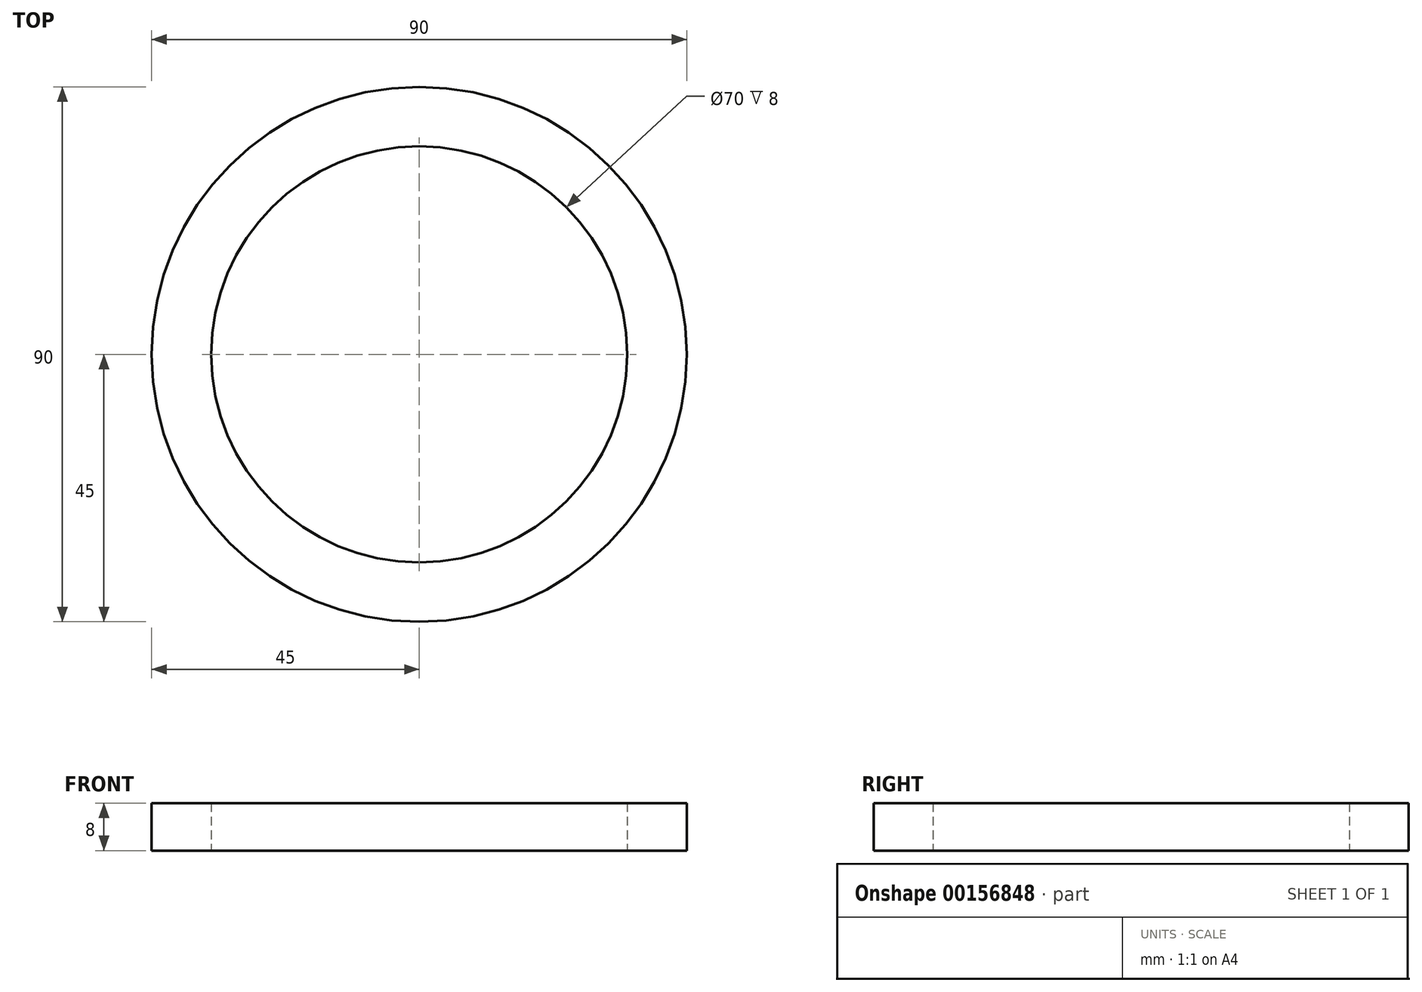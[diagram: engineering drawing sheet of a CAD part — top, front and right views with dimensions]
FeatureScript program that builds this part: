
annotation { "Feature Type Name" : "Feature", "Feature Type Description" : "" }
export const myFeature = defineFeature(function(context is Context, id is Id, definition is map)
    precondition{}
    {
        {
            var Q0;
            Q0=qCreatedBy(makeId("Top.planeOp"),FACE);
            var sketch = newSketch(context, id + "F0", { "sketchPlane" : qUnion([Q0])});
            skCircle(sketch, "E0", {"center": v(0, 0) * mm, "radius": 35 * mm});
            skCircle(sketch, "E1", {"center": v(0, 0) * mm, "radius": 45 * mm});
            skSolve(sketch);
        }
        {
            var Q0;
            Q0=makeQuery(id+"F0.imprint","IMPRINT",FACE,{"disambiguationData":[TD([[makeQuery(id+"F0.imprint","IMPRINT",EDGE,{"derivedFrom":sQuery(id+"F0.wireOp",EDGE,"E0")}),-1.0]])]});
            extrude(context, id + "F1", {"entities" : qUnion([Q0]), "depth" : 8 * mm});
        }
    });
